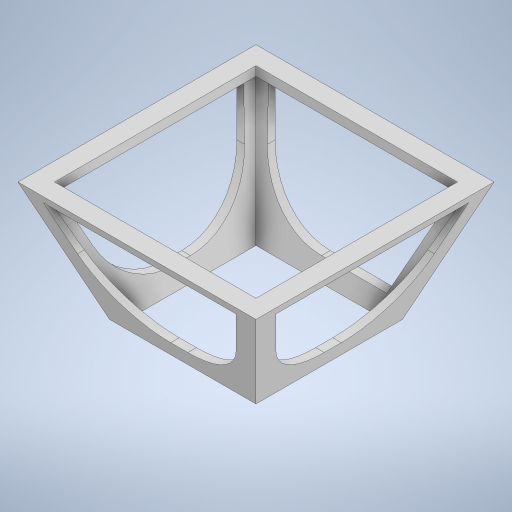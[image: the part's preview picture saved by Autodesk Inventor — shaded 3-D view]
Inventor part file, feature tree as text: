
AUTODESK INVENTOR PART (.ipt)
format: ipt  version: 2023 (Build 270158000, 158)  size: 335,872 bytes
history: native  units: mm
features: sketch x7, plane x4, extrude x3, loft x2, fillet x1
ambient origin geometry x8: Origin, YZ Plane, XZ Plane, XY Plane, X Axis, Y Axis, Z Axis, Center Point
bodies: Solid1 (feature_tree)
feature tree (17):
  sketch  "Sketch1"  dims[d0=80.0mm d1=80.0mm]
  plane  "Work Plane1"
  loft  "Loft1"
  sketch  "Sketch3"  dims[d10=130.0mm d13=130.0mm]
  plane  "Work Plane2"
  loft  "Loft2"
  plane  "Work Plane3"
  extrude  "Extrusion1"  Depth=130.0mm
  plane  "Work Plane4"
  extrude  "Extrusion2"  TaperAngle=0.0deg  [1 undecoded]
  fillet  "Fillet1"  [1 undecoded]
  extrude  "Extrusion3"  Depth=5.0mm
  sketch  "Sketch2"  dims[d6=70.0mm d9=30.0mm]
  sketch  "Sketch4"  dims[d15=30.0mm d16=0.0mm d17=90.0deg d18=0.0mm d19=90.0deg]
  sketch  "Sketch5"  dims[d20=5.0mm d21=5.0mm]
  sketch  "Sketch6"  dims[d22=5.0mm]
  sketch  "Sketch7"  dims[d23=5.0mm d24=-5.0mm d25=5.0mm d26=5.0mm d27=0.0mm d28=90.0deg d29=0.0mm d30=90.0deg d31=35.5mm d32=10.0mm d34=5.0mm d36=10.0mm d37=10.0mm d38=0.0mm d39=0.0mm d40=65.0mm d41=5.0mm d43=10.0mm d44=10.0mm d45=10.0mm d46=10.0mm d47=0.0mm d48=40.0mm d49=10.0mm d50=10.0mm d51=10.0mm d52=10.0mm d53=10.0mm d54=0.0mm]
note: 2 required parameter values undecoded (feature->parameter linkage not recoverable at this tier; creation-order binding heuristic only, values carry confidence <= 0.55)
